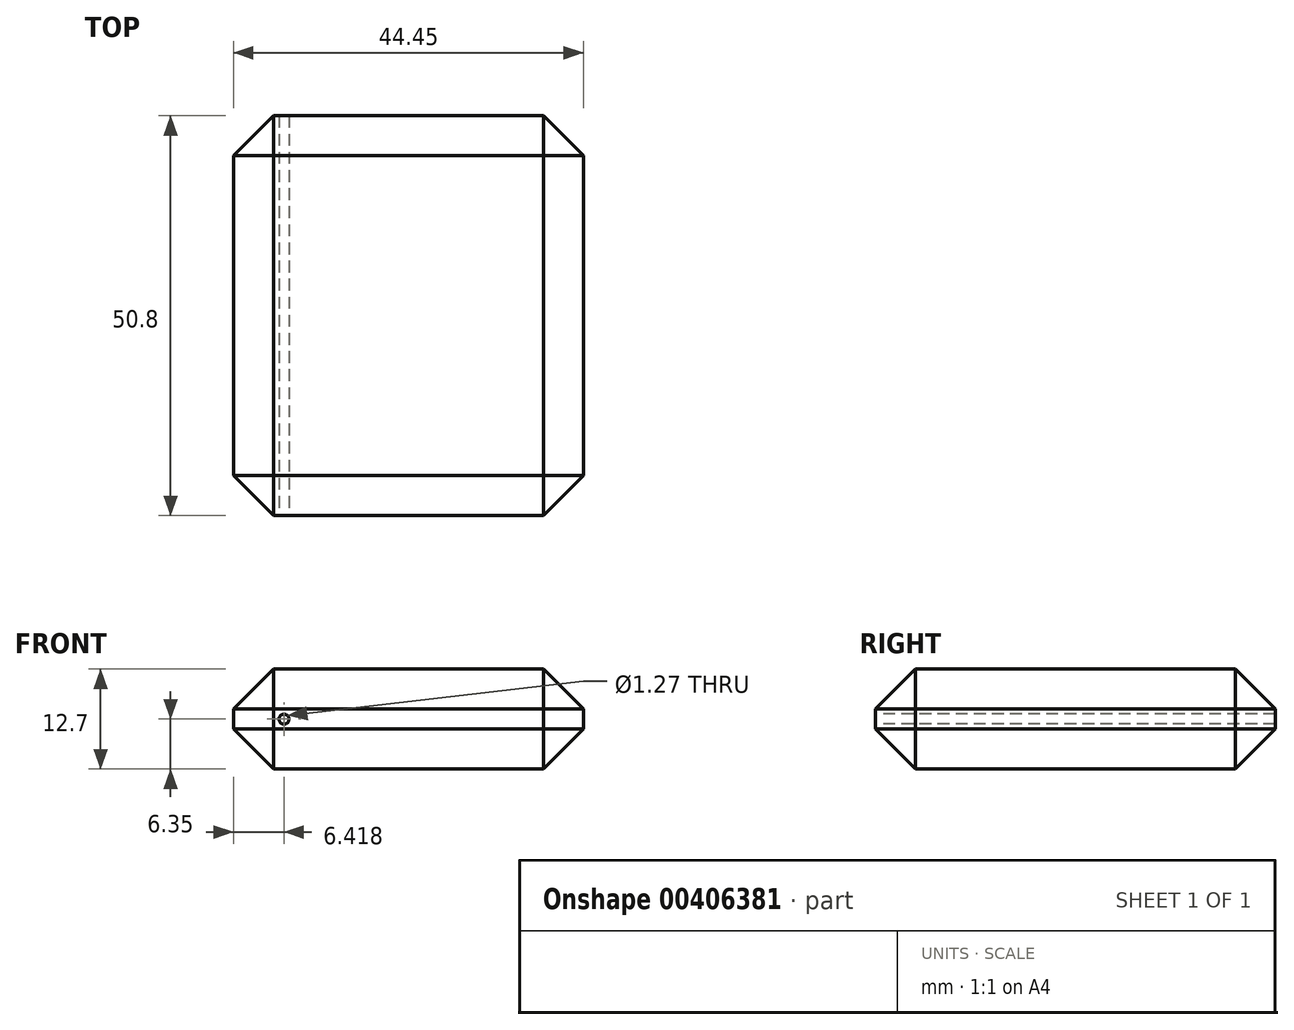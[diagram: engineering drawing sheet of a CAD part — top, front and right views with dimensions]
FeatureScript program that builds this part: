
annotation { "Feature Type Name" : "Feature", "Feature Type Description" : "" }
export const myFeature = defineFeature(function(context is Context, id is Id, definition is map)
    precondition{}
    {
        {
            var Q0;
            Q0=qCreatedBy(makeId("Top.planeOp"),FACE);
            var sketch = newSketch(context, id + "F0", { "sketchPlane" : qUnion([Q0])});
            skLineSegment(sketch, "E0.bottom", {"start": v(-45.11, -40.24) * mm, "end": v(-0.66, -40.24) * mm});
            skLineSegment(sketch, "E0.top", {"start": v(-45.11, 10.56) * mm, "end": v(-0.66, 10.56) * mm});
            skLineSegment(sketch, "E0.left", {"start": v(-45.11, -40.24) * mm, "end": v(-45.11, 10.56) * mm});
            skLineSegment(sketch, "E0.right", {"start": v(-0.66, -40.24) * mm, "end": v(-0.66, 10.56) * mm});
            skSolve(sketch);
        }
        {
            var Q0;
            Q0=makeQuery(id+"F0.imprint","IMPRINT",FACE,{"disambiguationData":[TD([[makeQuery(id+"F0.imprint","IMPRINT",EDGE,{"derivedFrom":sQuery(id+"F0.wireOp",EDGE,"E0.bottom")}),1.0]])]});
            extrude(context, id + "F1", {"entities" : qUnion([Q0]), "depth" : 12.7 * mm});
        }
        {
            var Q0;
            Q0=makeQuery(id+"F1.opExtrude","CAP_FACE",FACE,{"disambiguationData":[OSD([sQuery(id+"F0.wireOp",EDGE,"E0.bottom"),sQuery(id+"F0.wireOp",EDGE,"E0.top"),sQuery(id+"F0.wireOp",EDGE,"E0.left"),sQuery(id+"F0.wireOp",EDGE,"E0.right")])],"isStart":false});
            var Q1;
            Q1=makeQuery(id+"F1.opExtrude","CAP_EDGE",EDGE,{"disambiguationData":[OSD([sQuery(id+"F0.wireOp",EDGE,"E0.left")])],"isStart":true});
            var Q2;
            Q2=makeQuery(id+"F1.opExtrude","CAP_EDGE",EDGE,{"disambiguationData":[OSD([sQuery(id+"F0.wireOp",EDGE,"E0.bottom")])],"isStart":true});
            var Q3;
            Q3=makeQuery(id+"F1.opExtrude","CAP_EDGE",EDGE,{"disambiguationData":[OSD([sQuery(id+"F0.wireOp",EDGE,"E0.right")])],"isStart":true});
            var Q4;
            Q4=makeQuery(id+"F1.opExtrude","SWEPT_FACE",FACE,{"disambiguationData":[OSD([sQuery(id+"F0.wireOp",EDGE,"E0.top")])]});
            var Q5;
            Q5=makeQuery(id+"F1.opExtrude","SWEPT_EDGE",EDGE,{"disambiguationData":[OSD([sQuery(id+"F0.wireOp",EDGE,"E0.bottom"),sQuery(id+"F0.wireOp",EDGE,"E0.right")])]});
            var Q6;
            Q6=makeQuery(id+"F1.opExtrude","SWEPT_EDGE",EDGE,{"disambiguationData":[OSD([sQuery(id+"F0.wireOp",EDGE,"E0.bottom"),sQuery(id+"F0.wireOp",EDGE,"E0.left")])]});
            chamfer(context, id + "F2", {"entities" : qUnion([Q0, Q1, Q2, Q3, Q4, Q5, Q6]), "width" : 5.08 * mm, "tangentPropagation" : true});
        }
        {
            var Q0;
            Q0=makeQuery(id+"F1.opExtrude","SWEPT_FACE",FACE,{"disambiguationData":[OSD([sQuery(id+"F0.wireOp",EDGE,"E0.bottom")])]});
            var sketch = newSketch(context, id + "F3", { "sketchPlane" : qUnion([Q0])});
            skPoint(sketch, "E1", {"position": v(-38.7, 5.08) * mm});
            skPoint(sketch, "E2", {"position": v(-38.7, 6.35) * mm});
            skPoint(sketch, "E2.positionSnap0", {"position": v(-40.03, 6.35) * mm});
            skSolve(sketch);
        }
        {
            var Q0;
            Q0=sQuery(id+"F3.wireOp",VERTEX,"E2");
            var Q1;
            Q1=makeQuery(id+"F1.opExtrude","SWEPT_BODY",BODY,{"disambiguationData":[OSD([sQuery(id+"F0.wireOp",EDGE,"E0.bottom"),sQuery(id+"F0.wireOp",EDGE,"E0.top"),sQuery(id+"F0.wireOp",EDGE,"E0.left"),sQuery(id+"F0.wireOp",EDGE,"E0.right")])]});
            hole(context, id + "F4", {"style" : HoleStyle.SIMPLE, "endStyle" : HoleEndStyle.THROUGH, "holeDiameter" : 1.27 * mm, "isTappedThrough" : true, "tappedDepth" : 12.7 * mm, "tapClearance" : 3, "locations" : qUnion([Q0]), "scope" : qUnion([Q1])});
        }
    });
